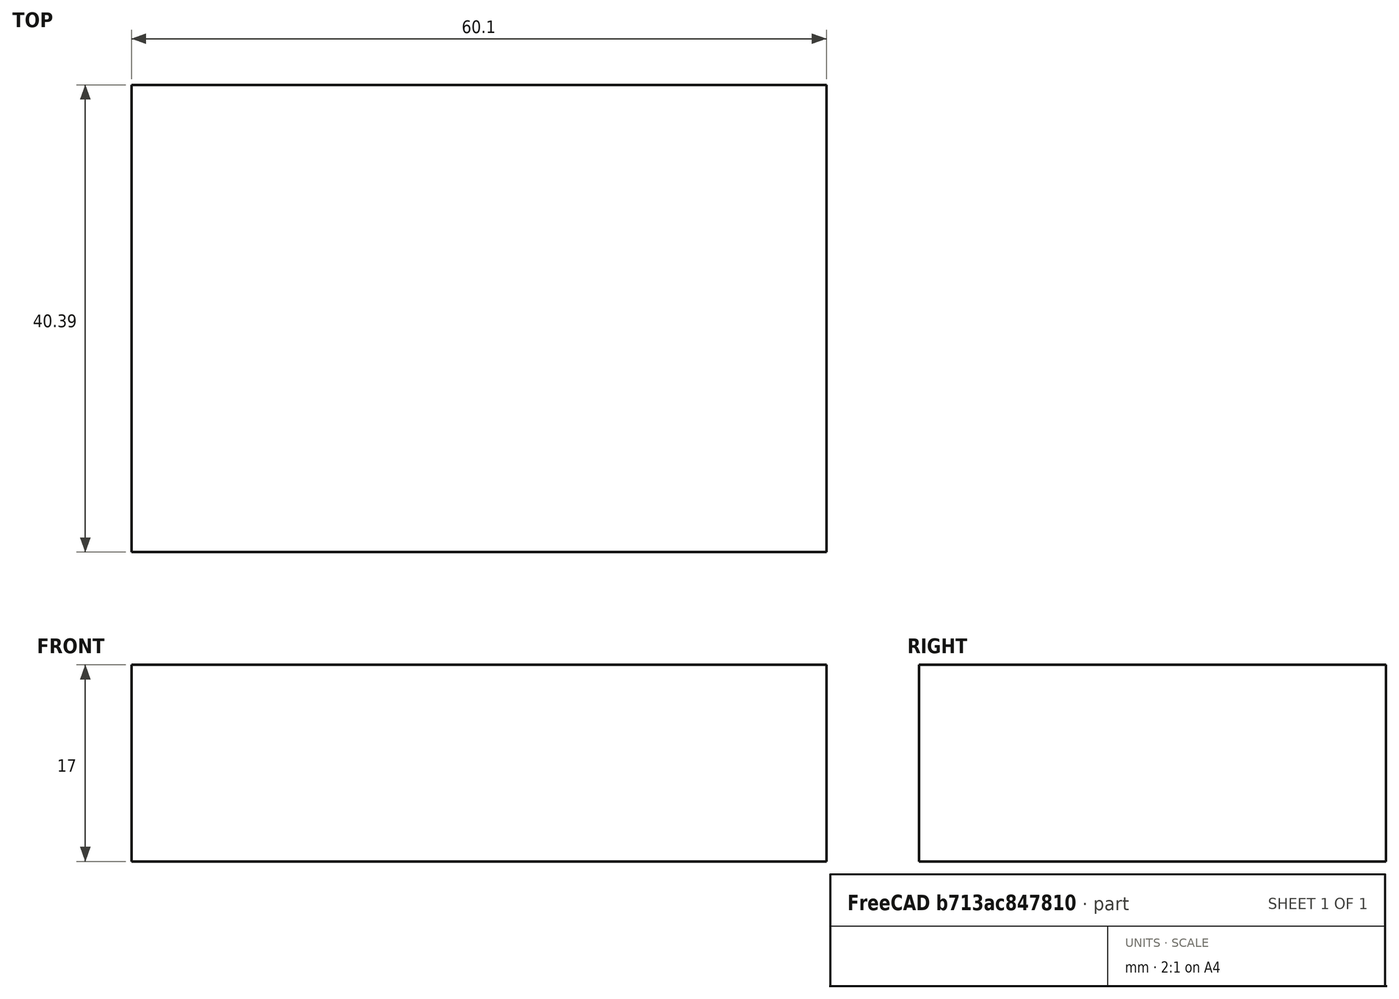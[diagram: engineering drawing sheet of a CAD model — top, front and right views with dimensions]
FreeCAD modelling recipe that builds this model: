
FCSTD DOCUMENT  (FreeCAD 0.20R29410 (Git))
Label: group
License: All rights reserved
LicenseURL: http://en.wikipedia.org/wiki/All_rights_reserved
objects: App::DocumentObjectGroupPython×5, App::FeaturePython×4, Sketcher::SketchObject×1, PartDesign::Pad×1, PartDesign::Body×1
note: 4 computed .brp shape members not serialized (recipe doc carries the construction recipe); baked Part::Feature solids carry a one-line shape summary decoded from their .brp

FEATURE [Sketcher::SketchObject] Sketch
  FullyConstrained = false
  MapMode = 5
  Support = -> [XY_Plane]
  sketch-geometry (4):
    g0: LineSegment StartX=0 StartY=0 StartZ=0 EndX=60.0985 EndY=0 EndZ=0
    g1: LineSegment StartX=60.0985 StartY=0 StartZ=0 EndX=60.0985 EndY=40.3941 EndZ=0
    g2: LineSegment StartX=60.0985 StartY=40.3941 StartZ=0 EndX=0 EndY=40.3941 EndZ=0
    g3: LineSegment StartX=0 StartY=40.3941 StartZ=0 EndX=0 EndY=0 EndZ=0
  constraints (9):
    c: Coincident(g0,g1)
    c: Coincident(g1,g2)
    c: Coincident(g2,g3)
    c: Coincident(g3,g0)
    c: Horizontal(g0)
    c: Horizontal(g2)
    c: Vertical(g1)
    c: Vertical(g3)
    c: Coincident(g0,g-1)
FEATURE [PartDesign::Pad] Pad
  Direction = (0,0,1)
  Length = 17
  Length2 = 10
  Profile = -> Sketch
  ReferenceAxis = -> Sketch [N_Axis]
  Type = 0
FEATURE [PartDesign::Body] Body
  Group = -> [Sketch,Pad]
  Origin = -> Origin
  Tip = -> Pad
FEATURE [App::FeaturePython] AnnotationPlane  label="AP1"  # WARN: FeaturePython — macro-defined, semantics opaque (R4)
  Direction = (0,0,1)
  PointWithOffset = (30.0493,20.197,17)
  faces = -> Pad [Face6]
  p1 = (30.0493,20.197,17)
FEATURE [App::FeaturePython] DatumFeature  label="A"  # WARN: FeaturePython — macro-defined, semantics opaque (R4)
FEATURE [App::DocumentObjectGroupPython] Annotation1  # scripted group (container) (typed FeaturePython)
  AP = -> AnnotationPlane
  DF = -> DatumFeature
  Direction = (0,0,1)
  Group = -> [DatumFeature]
  circumferenceBool = false
  diameter = 0
  faces = -> [Pad]
  highLimit = 0
  lowLimit = 0
  p1 = (30.0493,20.197,17)
  selectedPoint = (30.0493,51.197,17)
  spBool = true
  toleranceDiameter = 0
  toleranceSelectBool = true
FEATURE [App::FeaturePython] DatumSystem  label="DS1: A"  # WARN: FeaturePython — macro-defined, semantics opaque (R4)
  Primary = -> DatumFeature
FEATURE [App::DocumentObjectGroupPython] DS  # scripted group (container) (typed FeaturePython)
  Group = -> [DatumSystem]
FEATURE [App::FeaturePython] GeometricTolerance  label="GT1"  # WARN: FeaturePython — macro-defined, semantics opaque (R4)
  Characteristic = Flatness
  CharacteristicCode = ⏥
  CharacteristicIcon = :/dd/icons/Characteristic/flatness.svg
  Circumference = false
  ToleranceValue = 0.2
FEATURE [App::DocumentObjectGroupPython] Annotation2  # scripted group (container) (typed FeaturePython)
  AP = -> AnnotationPlane
  Direction = (0,0,1)
  GT = -> [GeometricTolerance]
  Group = -> [GeometricTolerance]
  circumferenceBool = false
  diameter = 0
  faces = -> [Pad]
  highLimit = 0
  lowLimit = 0
  p1 = (30.0493,20.197,17)
  selectedPoint = (-40,-22,0)
  spBool = true
  toleranceDiameter = 0
  toleranceSelectBool = true
FEATURE [App::DocumentObjectGroupPython] Plane_AP1  # scripted group (container) (typed FeaturePython)
  Group = -> [AnnotationPlane,Annotation2,Annotation1]
FEATURE [App::DocumentObjectGroupPython] GDT  # scripted group (container) (typed FeaturePython)
  Group = -> [DS,Plane_AP1]
